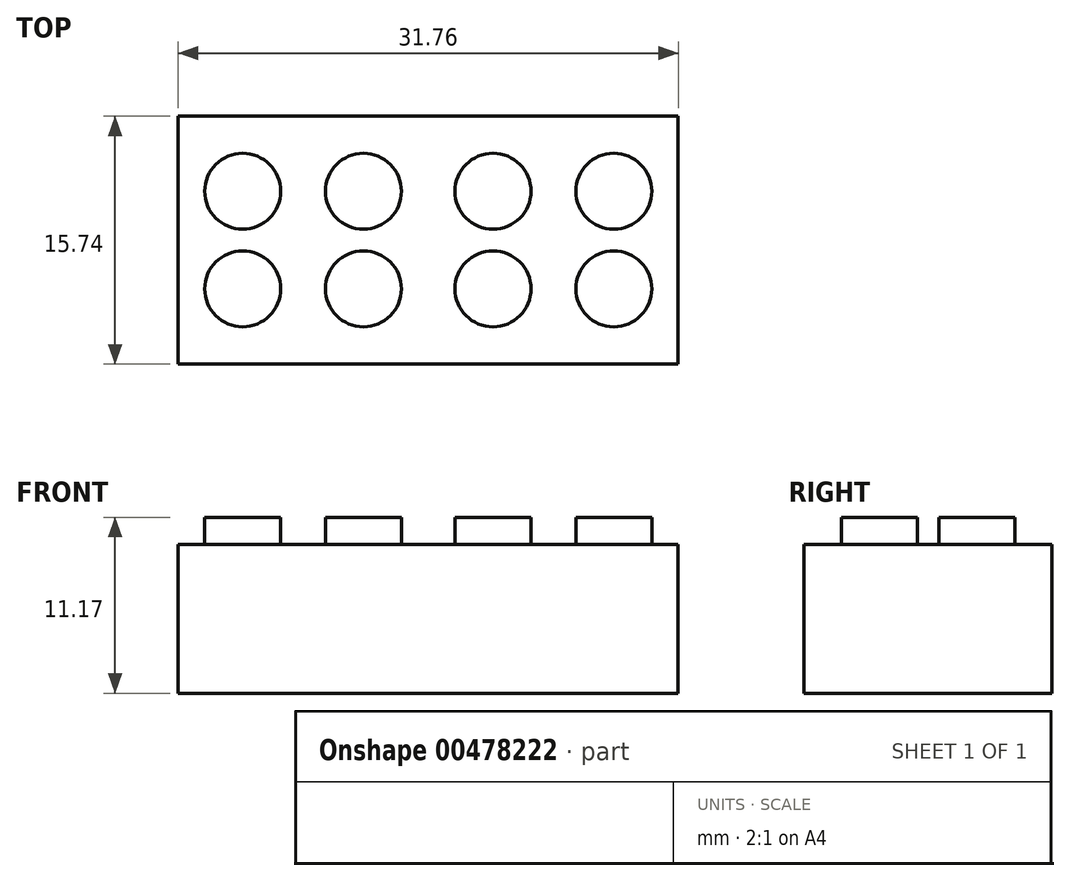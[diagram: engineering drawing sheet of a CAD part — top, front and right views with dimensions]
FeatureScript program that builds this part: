
annotation { "Feature Type Name" : "Feature", "Feature Type Description" : "" }
export const myFeature = defineFeature(function(context is Context, id is Id, definition is map)
    precondition{}
    {
        {
            var Q0;
            Q0=qCreatedBy(makeId("Top.planeOp"),FACE);
            var sketch = newSketch(context, id + "F0", { "sketchPlane" : qUnion([Q0])});
            skLineSegment(sketch, "E0.bottom", {"start": v(15.88, 7.87) * mm, "end": v(-15.88, 7.87) * mm});
            skLineSegment(sketch, "E0.top", {"start": v(15.88, -7.87) * mm, "end": v(-15.87, -7.87) * mm});
            skLineSegment(sketch, "E0.left", {"start": v(15.88, 7.87) * mm, "end": v(15.88, -7.87) * mm});
            skLineSegment(sketch, "E0.right", {"start": v(-15.88, 7.87) * mm, "end": v(-15.88, -7.87) * mm});
            skPoint(sketch, "E0.middle", {"position": v(0, 0) * mm});
            skSolve(sketch);
        }
        {
            var Q0;
            Q0 = qSketchRegion(id + "F0", true);
            extrude(context, id + "F1", {"entities" : qUnion([Q0]), "endBound" : BoundingType.SYMMETRIC, "depth" : 9.45 * mm});
        }
        {
            var Q0;
            Q0=makeQuery(id+"F1.opExtrude","CAP_FACE",FACE,{"disambiguationData":[OSD([sQuery(id+"F0.wireOp",EDGE,"E0.bottom"),sQuery(id+"F0.wireOp",EDGE,"E0.top"),sQuery(id+"F0.wireOp",EDGE,"E0.left"),sQuery(id+"F0.wireOp",EDGE,"E0.right")])],"isStart":false});
            var sketch = newSketch(context, id + "F2", { "sketchPlane" : qUnion([Q0])});
            skCircle(sketch, "E1", {"center": v(-11.79, 3.1) * mm, "radius": 2.41 * mm});
            skCircle(sketch, "E2", {"center": v(4.11, 3.1) * mm, "radius": 2.41 * mm});
            skCircle(sketch, "E3", {"center": v(11.79, 3.1) * mm, "radius": 2.41 * mm});
            skCircle(sketch, "E4.MirrorC", {"center": v(-11.79, -3.1) * mm, "radius": 2.41 * mm});
            skCircle(sketch, "E5.MirrorC", {"center": v(4.11, -3.1) * mm, "radius": 2.41 * mm});
            skCircle(sketch, "E6.MirrorC", {"center": v(11.79, -3.1) * mm, "radius": 2.41 * mm});
            skCircle(sketch, "E7.MirrorC", {"center": v(-4.11, -3.1) * mm, "radius": 2.41 * mm});
            skCircle(sketch, "E8.MirrorC", {"center": v(-4.11, 3.1) * mm, "radius": 2.41 * mm});
            skSolve(sketch);
        }
        {
            var Q0;
            Q0 = qSketchRegion(id + "F2", true);
            extrude(context, id + "F3", {"entities" : qUnion([Q0]), "operationType" : NewBodyOperationType.ADD, "depth" : 1.73 * mm});
        }
    });
